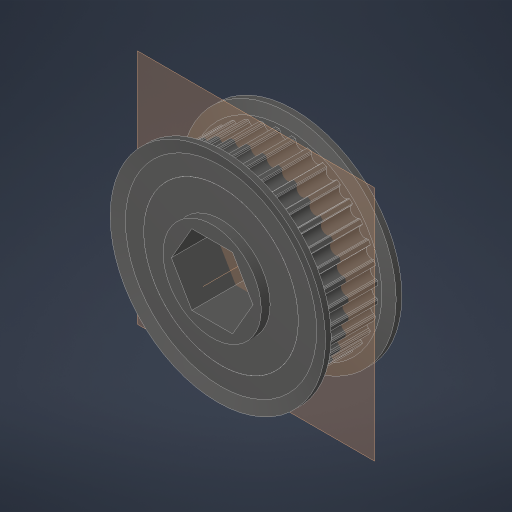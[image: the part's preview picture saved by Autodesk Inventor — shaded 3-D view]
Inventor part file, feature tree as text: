
AUTODESK INVENTOR PART (.ipt)
format: ipt  version: 2023.4 (Build 274418000, 418)  size: 486,912 bytes
history: native  units: in
note: dims shown in document units (in); Inventor stores cm internally (conversion verified against a paired STEP export)
features: revolve x2, other x1
ambient origin geometry x8: Origin, YZ Plane, XZ Plane, XY Plane, X Axis, Y Axis, Z Axis, Center Point
bodies: Solid1 (feature_tree), Solid2 (feature_tree), Solid3 (feature_tree)
feature tree (3):
  revolve  "Revolve1[1]"  [1 undecoded]
  revolve  "Revolve1[2]"  [1 undecoded]
  other  "Cut-Extrude4"
note: 2 required parameter values undecoded (feature->parameter linkage not recoverable at this tier; creation-order binding heuristic only, values carry confidence <= 0.55)
